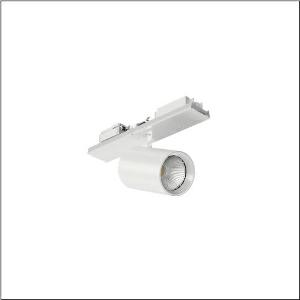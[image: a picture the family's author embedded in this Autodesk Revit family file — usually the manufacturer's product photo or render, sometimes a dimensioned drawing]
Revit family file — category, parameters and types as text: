
# Revit family: licross_r__spot_31_51sl127a43b_2c6e
name_source: partatom
category: Lighting Fixtures
units: mm (PartAtom-declared; Revit-internal decimal feet)

## family parameters
Cut with Voids When Loaded = No
Host = Face
Light Source = No
Part Type = Normal
Room Calculation Point = No
Round Connector Dimension = Use Diameter
Shared = No

## types (1)
- --- (1 x LED, 3650 lm, 28 W, 4000K)
    Apparent Load = 28 VA
    CIE Flux Codes = 93 97 99 100 100
    Color Rendering = 90
    Color Temperature = 4000K
    Default Elevation = 1800 mm
    Description = Licross® Spot 31, directional spotlight, light control with lens, of plastic, LED rated luminous flux: 3.650lm, light colour: 940, with plug, 3-pole, with phase selection, mains connection: 220..240V, AC, 50/60Hz, of aluminium, traffic white (RAL 9016), length: 140mm, diameter: 90mm, protection rating (complete): IP20, insulation class (complete): insulation class I (protective earthing), certification: CE, packaging unit: 1 piece
    Height = 175 mm
    Lamp = 1 x LED
    Lamp Light Flux = 3650 lm
    Lamp Power = 28 W
    Lamp count = 1
    Length = 90 mm
    Luminous efficacy = 130 lm/W
    Manufacturer = Siteco
    ModVariant = No
    Model = 51SL127A43B
    Mounting Place = Ceiling
    Mounting Type = Pendant
    Number of Poles = 1
    OnlyDefault = Yes
    Power Factor = 1
    Product Name = Licross® Spot 31
    Product group = directional spotlight
    ProductGroupID = 905
    Protection Class = Protection class I
    Protection Degree = IP 20
    RLX_Detail_Level = 1
    RLX_Emergency_Light_Flux = 0 lm
    RLX_Emergency_Type = 0
    RLX_Emergency_Type_DB = No
    RlxData = <blob elided: 14897 chars, md5=18d70bca>
    Socket = socket
    Standby Power = 0 W
    System Light Flux = 3650 lm
    System Power = 28 W
    Type Comments = factory setting: luminous flux: 100 % | (ON | ON | ON) | 700 mA
    Type Image = l_1245720.jpg
    URL = http://relux.com
    VarID = @adj_064119
    Voltage = 0 V
    Weight = 0.00 kg
    Width = 0 mm  [stored 0 ft]

note: [stored X ft] marks values corroborated as IEEE doubles in the binary element streams (Revit-internal decimal feet)

## geometry (parser evidence)
native form markers: Sweep x10
no freeform markers — native parametric forms only
